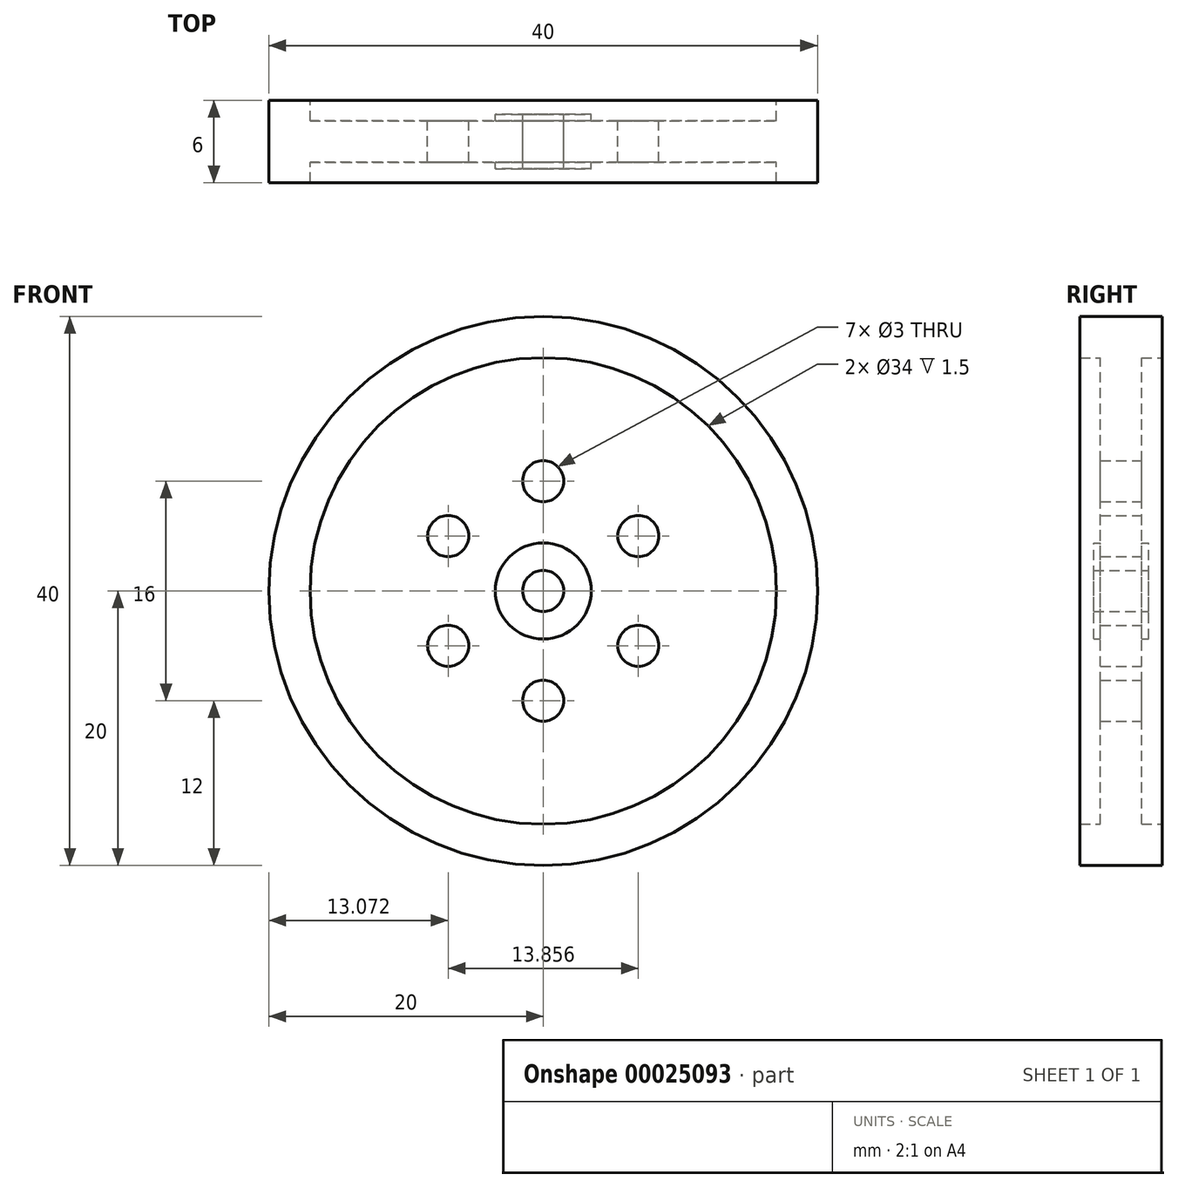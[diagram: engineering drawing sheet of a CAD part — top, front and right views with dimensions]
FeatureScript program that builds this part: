
annotation { "Feature Type Name" : "Feature", "Feature Type Description" : "" }
export const myFeature = defineFeature(function(context is Context, id is Id, definition is map)
    precondition{}
    {
        {
            var Q0;
            Q0=qCreatedBy(makeId("Front.planeOp"),FACE);
            var sketch = newSketch(context, id + "F0", { "sketchPlane" : qUnion([Q0])});
            skCircle(sketch, "E0", {"center": v(0, 0) * mm, "radius": 17 * mm});
            skCircle(sketch, "E1", {"center": v(0, 0) * mm, "radius": 20 * mm});
            skCircle(sketch, "E2", {"center": v(0, 0) * mm, "radius": 3.5 * mm});
            skCircle(sketch, "E3", {"center": v(0, 0) * mm, "radius": 1.5 * mm});
            skCircle(sketch, "E4", {"center": v(0, 8) * mm, "radius": 1.5 * mm});
            skCircle(sketch, "E5.1.0", {"center": v(-6.93, 4) * mm, "radius": 1.5 * mm});
            skCircle(sketch, "E5.2.0", {"center": v(-6.93, -4) * mm, "radius": 1.5 * mm});
            skCircle(sketch, "E5.3.0", {"center": v(0, -8) * mm, "radius": 1.5 * mm});
            skCircle(sketch, "E5.4.0", {"center": v(6.93, -4) * mm, "radius": 1.5 * mm});
            skCircle(sketch, "E5.5.0", {"center": v(6.93, 4) * mm, "radius": 1.5 * mm});
            skSolve(sketch);
        }
        {
            var Q0;
            Q0=makeQuery(id+"F0.imprint","IMPRINT",FACE,{"disambiguationData":[TD([[makeQuery(id+"F0.imprint","IMPRINT",EDGE,{"derivedFrom":sQuery(id+"F0.wireOp",EDGE,"E0")}),1.0]])]});
            extrude(context, id + "F1", {"entities" : qUnion([Q0]), "endBound" : BoundingType.SYMMETRIC, "depth" : 3 * mm});
        }
        {
            var Q0;
            Q0 = qSketchRegion(id + "F0", true);
            extrude(context, id + "F2", {"entities" : qUnion([Q0]), "operationType" : NewBodyOperationType.ADD, "endBound" : BoundingType.SYMMETRIC, "depth" : 6 * mm, "hasSecondDirection" : true, "secondDirectionOppositeDirection" : true, "secondDirectionDepth" : 6 * mm});
        }
        {
            var Q0;
            Q0=makeQuery(id+"F0.imprint","IMPRINT",FACE,{"disambiguationData":[TD([[makeQuery(id+"F0.imprint","IMPRINT",EDGE,{"derivedFrom":sQuery(id+"F0.wireOp",EDGE,"E2")}),1.0]])]});
            extrude(context, id + "F3", {"entities" : qUnion([Q0]), "operationType" : NewBodyOperationType.ADD, "endBound" : BoundingType.SYMMETRIC, "depth" : 4 * mm, "hasSecondDirection" : true, "secondDirectionOppositeDirection" : true, "secondDirectionDepth" : 4 * mm});
        }
    });
